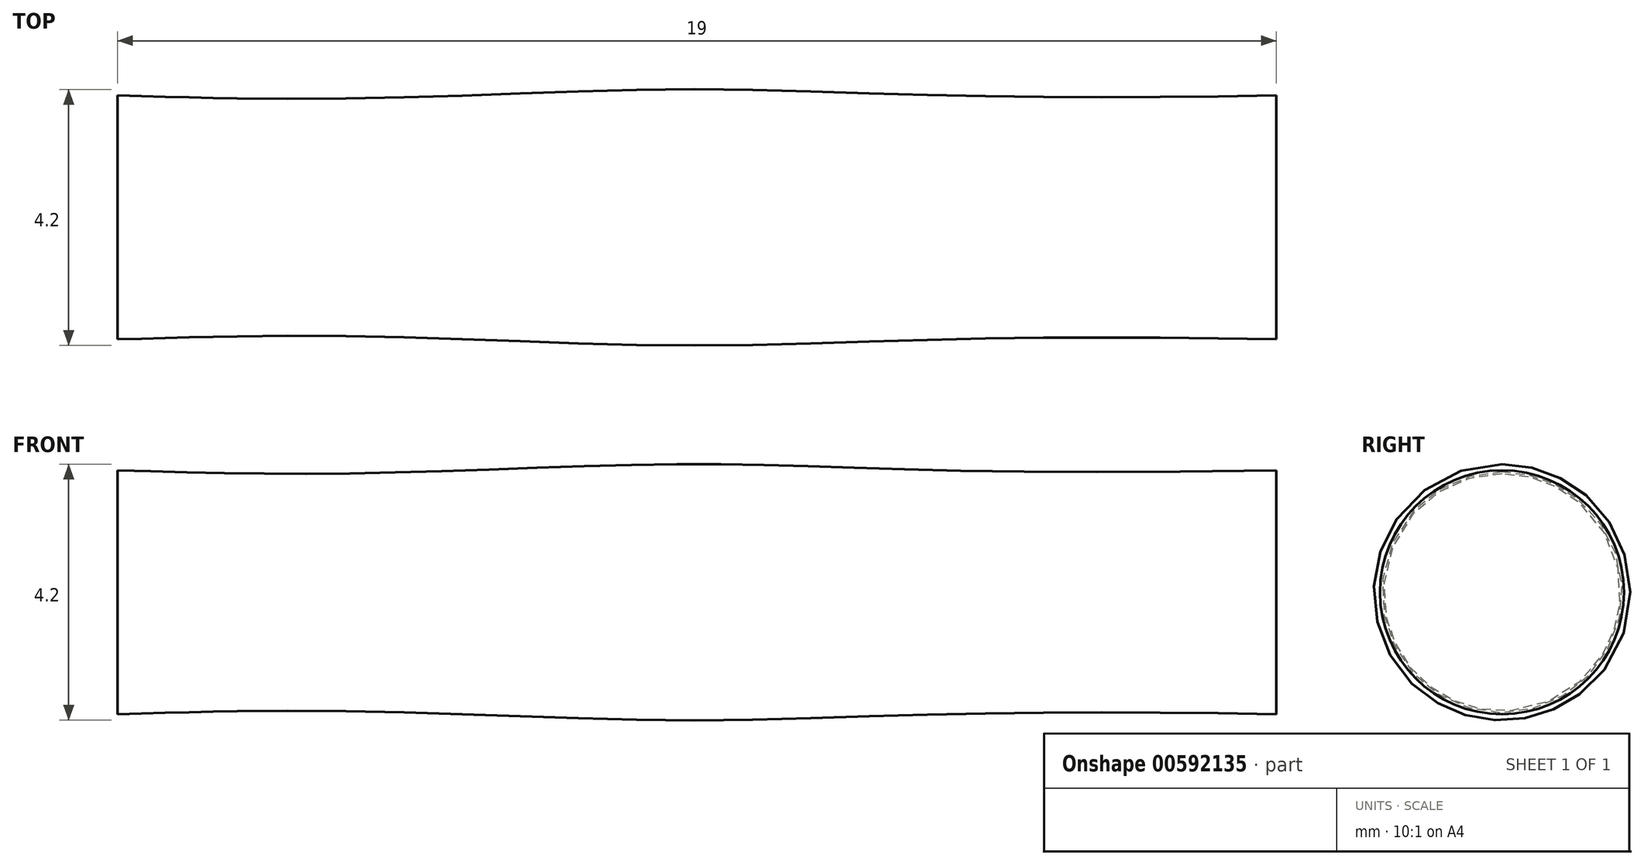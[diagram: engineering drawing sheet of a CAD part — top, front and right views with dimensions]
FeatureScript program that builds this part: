
annotation { "Feature Type Name" : "Feature", "Feature Type Description" : "" }
export const myFeature = defineFeature(function(context is Context, id is Id, definition is map)
    precondition{}
    {
        {
            var Q0;
            Q0=qCreatedBy(makeId("Top.planeOp"),FACE);
            var sketch = newSketch(context, id + "F0", { "sketchPlane" : qUnion([Q0])});
            skLineSegment(sketch, "E0", {"start": v(-19, 0) * mm, "end": v(19, 0) * mm});
            skLineSegment(sketch, "E1", {"start": v(-19, 0) * mm, "end": v(-19, 4) * mm});
            skLineSegment(sketch, "E2", {"start": v(19, 0) * mm, "end": v(19, 4) * mm});
            skFitSpline(sketch, "E3", {"points": [v(-19, 4) * mm, v(-11.22, 3.9) * mm, v(0, 4.2) * mm, v(19, 4) * mm], "startDerivative": vector(24.36, -0.67) * mm, "endDerivative": vector(77.52, 1.51) * mm});
            skSolve(sketch);
        }
        {
            var Q0;
            Q0 = qSketchRegion(id + "F0", true);
            var Q1;
            Q1=sQuery(id+"F0.wireOp",EDGE,"E0");
            revolve(context, id + "F1", {"entities" : qUnion([Q0]), "axis" : qUnion([Q1]), "revolveType" : RevolveType.FULL});
        }
        {
            var Q0;
            Q0=makeQuery(id+"F1.opRevolve","SWEPT_BODY",BODY,{"disambiguationData":[OSD([sQuery(id+"F0.wireOp",EDGE,"E0"),sQuery(id+"F0.wireOp",EDGE,"E1"),sQuery(id+"F0.wireOp",EDGE,"E2"),sQuery(id+"F0.wireOp",EDGE,"E3")])]});
            var Q1;
            Q1=qCreatedBy(makeId("Origin.pointOp"),VERTEX);
            var Q2;
            Q2=qCreatedBy(makeId("Origin.pointOp"),VERTEX);
            transform(context, id + "F2", {"entities" : qUnion([Q0]), "transformType" : TransformType.SCALE_UNIFORMLY, "scale" : .5, "scalePoint" : qUnion([Q2]), "makeCopy" : false});
        }
    });
